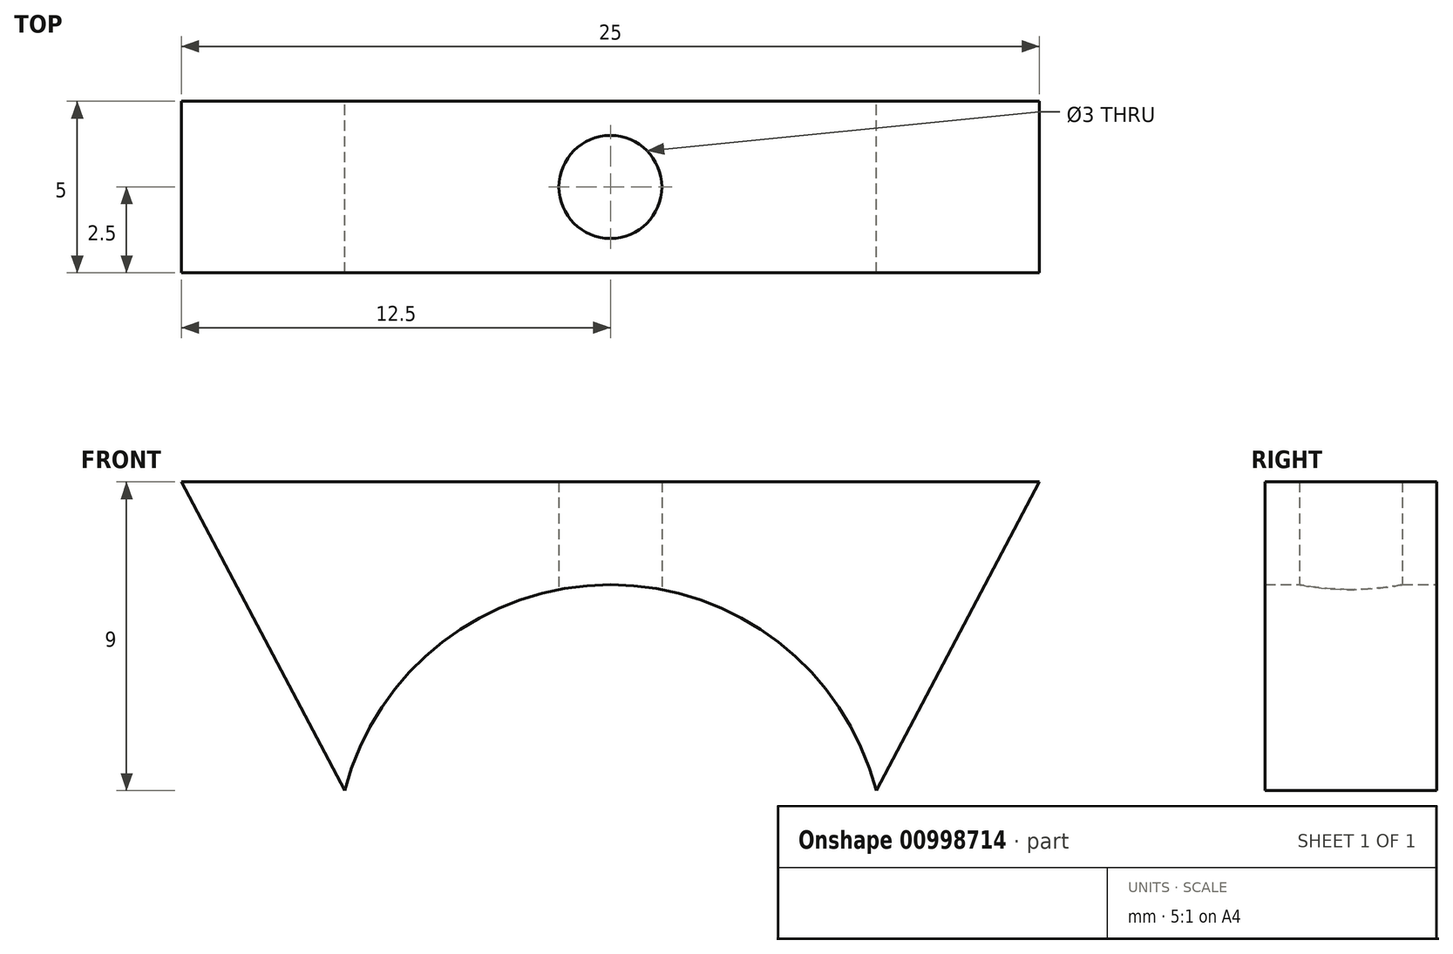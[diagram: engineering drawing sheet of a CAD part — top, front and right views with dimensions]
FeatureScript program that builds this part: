
annotation { "Feature Type Name" : "Feature", "Feature Type Description" : "" }
export const myFeature = defineFeature(function(context is Context, id is Id, definition is map)
    precondition{}
    {
        {
            var Q0;
            Q0=qCreatedBy(makeId("Front.planeOp"),FACE);
            var sketch = newSketch(context, id + "F0", { "sketchPlane" : qUnion([Q0])});
            skLineSegment(sketch, "E0", {"start": v(-12.5, 11) * mm, "end": v(12.5, 11) * mm});
            skLineSegment(sketch, "E1", {"start": v(0, 28.64) * mm, "end": v(0, -29.65) * mm, "construction": true});
            skPoint(sketch, "E2.start.orphan", {"position": v(-8, 0) * mm});
            skPoint(sketch, "E3.start.orphan", {"position": v(8, 0) * mm});
            skArc(sketch, "E4", {"start": v(7.75, 2) * mm, "mid": v(0, 8) * mm, "end": v(-7.75, 2) * mm});
            skLineSegment(sketch, "E5", {"start": v(-13.71, 2) * mm, "end": v(13.11, 2) * mm, "construction": true});
            skLineSegment(sketch, "E6", {"start": v(-12.5, 11) * mm, "end": v(-7.75, 2) * mm});
            skLineSegment(sketch, "E7", {"start": v(7.75, 2) * mm, "end": v(12.5, 11) * mm});
            skSolve(sketch);
        }
        {
            var Q0;
            Q0=makeQuery(id+"F0.imprint","IMPRINT",FACE,{"disambiguationData":[TD([[makeQuery(id+"F0.imprint","IMPRINT",EDGE,{"derivedFrom":sQuery(id+"F0.wireOp",EDGE,"qkrqzse2-mHjl-FPVe-h8ui-Bncq6iStuv0d")}),-1.0]])]});
            var Q1;
            Q1=makeQuery(id+"F0.imprint","IMPRINT",FACE,{"disambiguationData":[TD([[makeQuery(id+"F0.imprint","IMPRINT",EDGE,{"derivedFrom":sQuery(id+"F0.wireOp",EDGE,"E0")}),-1.0]])]});
            extrude(context, id + "F1", {"entities" : qUnion([Q0, Q1]), "endBound" : BoundingType.SYMMETRIC, "depth" : 5 * mm, "offsetDistance" : 25.4 * mm});
        }
        {
            var Q0;
            Q0=qCreatedBy(makeId("Top.planeOp"),FACE);
            var sketch = newSketch(context, id + "F2", { "sketchPlane" : qUnion([Q0])});
            skCircle(sketch, "E8", {"center": v(0, 0) * mm, "radius": 1.5 * mm});
            skSolve(sketch);
        }
        {
            var Q0;
            Q0=makeQuery(id+"F2.imprint","IMPRINT",FACE,{"disambiguationData":[TD([[makeQuery(id+"F2.imprint","IMPRINT",EDGE,{"derivedFrom":sQuery(id+"F2.wireOp",EDGE,"E8")}),1.0]])]});
            extrude(context, id + "F3", {"entities" : qUnion([Q0]), "operationType" : NewBodyOperationType.REMOVE, "endBound" : BoundingType.THROUGH_ALL, "depth" : 25 * mm, "offsetDistance" : 25 * mm});
        }
    });
